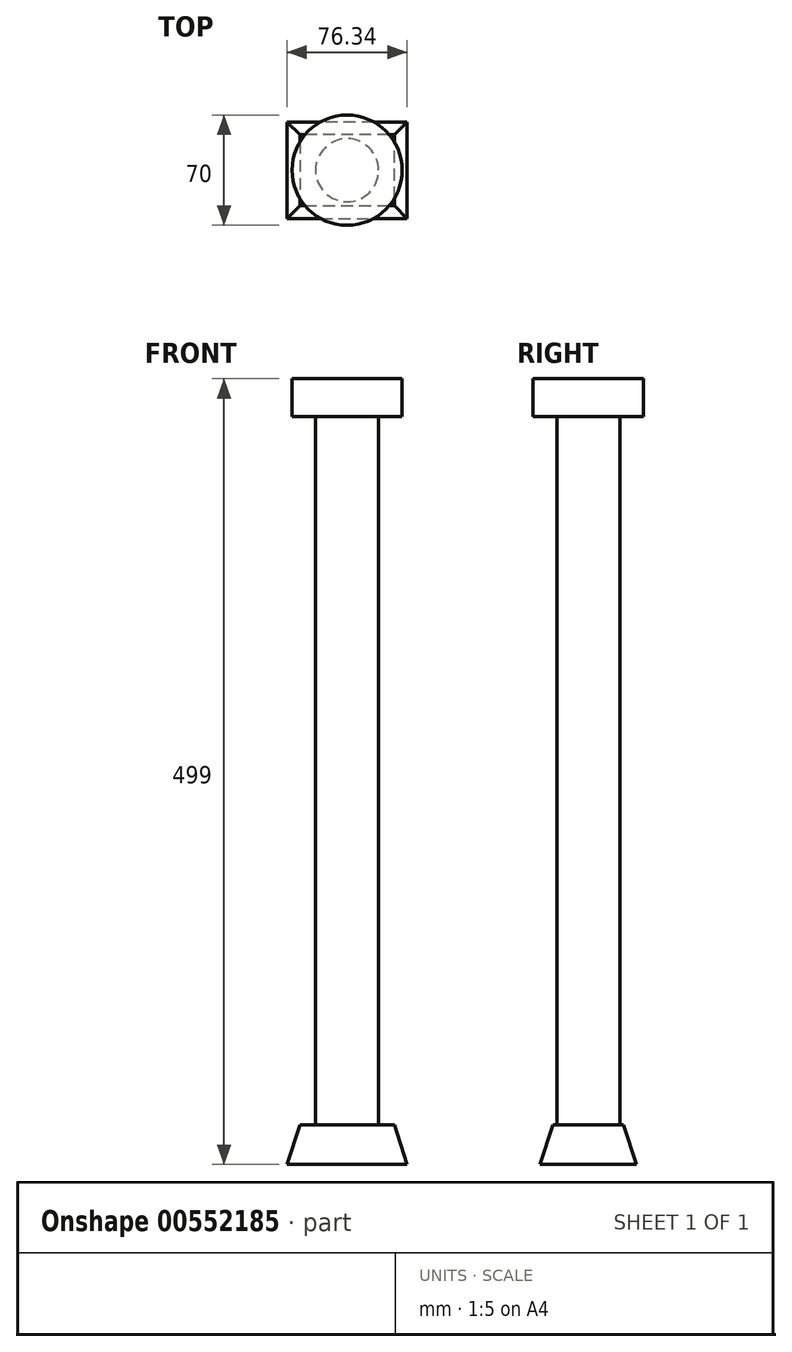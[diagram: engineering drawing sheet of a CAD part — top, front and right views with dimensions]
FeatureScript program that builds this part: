
annotation { "Feature Type Name" : "Feature", "Feature Type Description" : "" }
export const myFeature = defineFeature(function(context is Context, id is Id, definition is map)
    precondition{}
    {
        {
            var Q0;
            Q0=qCreatedBy(makeId("Top.planeOp"),FACE);
            var sketch = newSketch(context, id + "F0", { "sketchPlane" : qUnion([Q0])});
            skCircle(sketch, "E0", {"center": v(0, 0) * mm, "radius": 20 * mm});
            skSolve(sketch);
        }
        {
            var Q0;
            Q0 = qSketchRegion(id + "F0", true);
            extrude(context, id + "F1", {"entities" : qUnion([Q0]), "depth" : 450 * mm, "offsetDistance" : 25 * mm});
        }
        {
            var Q0;
            Q0=makeQuery(id+"F1.opExtrude","CAP_FACE",FACE,{"disambiguationData":[OSD([sQuery(id+"F0.wireOp",EDGE,"E0")])],"isStart":false});
            var sketch = newSketch(context, id + "F2", { "sketchPlane" : qUnion([Q0])});
            skCircle(sketch, "E1", {"center": v(0, 0) * mm, "radius": 35 * mm});
            skSolve(sketch);
        }
        {
            var Q0;
            Q0 = qSketchRegion(id + "F2", true);
            extrude(context, id + "F3", {"entities" : qUnion([Q0]), "operationType" : NewBodyOperationType.ADD, "depth" : 24 * mm, "offsetDistance" : 25 * mm});
        }
        {
            var Q0;
            Q0=qCreatedBy(makeId("Top.planeOp"),FACE);
            var sketch = newSketch(context, id + "F4", { "sketchPlane" : qUnion([Q0])});
            skLineSegment(sketch, "E2.bottom", {"start": v(-30, 22.5) * mm, "end": v(30, 22.5) * mm});
            skLineSegment(sketch, "E2.top", {"start": v(-30, -22.5) * mm, "end": v(30, -22.5) * mm});
            skLineSegment(sketch, "E2.left", {"start": v(-30, 22.5) * mm, "end": v(-30, -22.5) * mm});
            skLineSegment(sketch, "E2.right", {"start": v(30, 22.5) * mm, "end": v(30, -22.5) * mm});
            skPoint(sketch, "E2.middle", {"position": v(0, 0) * mm});
            skSolve(sketch);
        }
        {
            var Q0;
            Q0 = qSketchRegion(id + "F4", true);
            extrude(context, id + "F5", {"entities" : qUnion([Q0]), "operationType" : NewBodyOperationType.ADD, "oppositeDirection" : true, "depth" : 25 * mm, "offsetDistance" : 25 * mm, "hasDraft" : true, "draftAngle" : 18.1 * degree});
        }
    });
